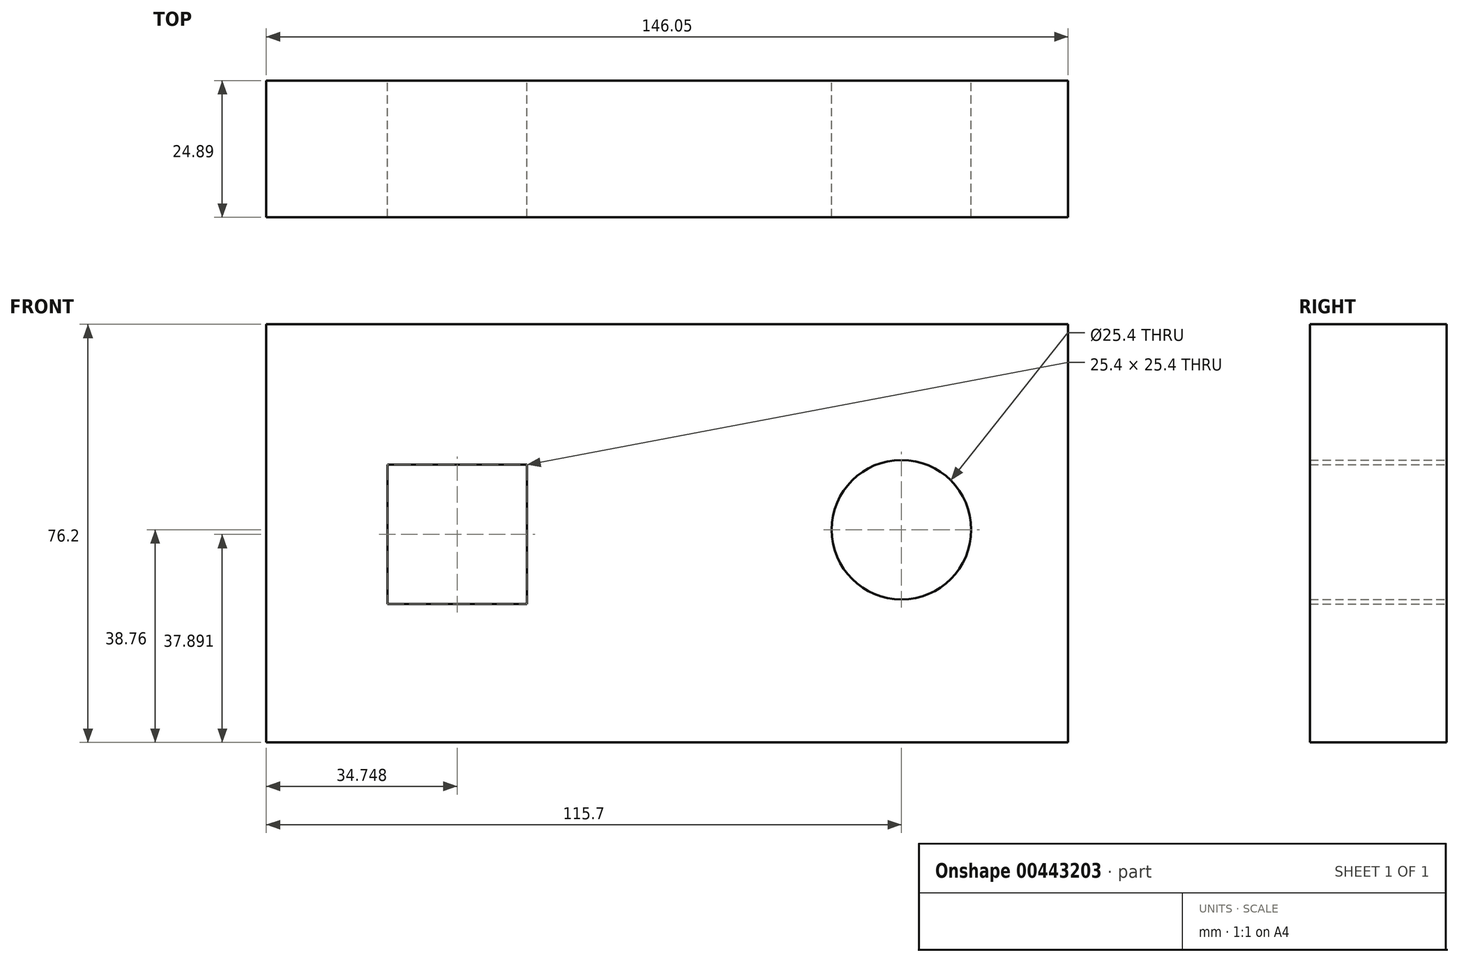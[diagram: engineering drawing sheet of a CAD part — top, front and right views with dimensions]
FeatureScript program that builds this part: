
annotation { "Feature Type Name" : "Feature", "Feature Type Description" : "" }
export const myFeature = defineFeature(function(context is Context, id is Id, definition is map)
    precondition{}
    {
        {
            var Q0;
            Q0=qCreatedBy(makeId("Front.planeOp"),FACE);
            var sketch = newSketch(context, id + "F0", { "sketchPlane" : qUnion([Q0])});
            skLineSegment(sketch, "E0.bottom", {"start": v(-115.7, 37.44) * mm, "end": v(30.35, 37.44) * mm});
            skLineSegment(sketch, "E0.top", {"start": v(-115.7, -38.76) * mm, "end": v(30.35, -38.76) * mm});
            skLineSegment(sketch, "E0.left", {"start": v(-115.7, 37.44) * mm, "end": v(-115.7, -38.76) * mm});
            skLineSegment(sketch, "E0.right", {"start": v(30.35, 37.44) * mm, "end": v(30.35, -38.76) * mm});
            skCircle(sketch, "E1", {"center": v(0, 0) * mm, "radius": 12.7 * mm});
            skLineSegment(sketch, "E2.bottom", {"start": v(-93.65, 11.83) * mm, "end": v(-68.25, 11.83) * mm});
            skLineSegment(sketch, "E2.top", {"start": v(-93.65, -13.57) * mm, "end": v(-68.25, -13.57) * mm});
            skLineSegment(sketch, "E2.left", {"start": v(-93.65, 11.83) * mm, "end": v(-93.65, -13.57) * mm});
            skLineSegment(sketch, "E2.right", {"start": v(-68.25, 11.83) * mm, "end": v(-68.25, -13.57) * mm});
            skPoint(sketch, "E3.orphan", {"position": v(-42.68, -38.76) * mm});
            skPoint(sketch, "E4.start.orphan", {"position": v(-42.68, 37.44) * mm});
            skPoint(sketch, "E5.orphan", {"position": v(0, 34.74) * mm});
            skPoint(sketch, "E6.trimOffspring.end.orphan", {"position": v(-81.26, -38.76) * mm});
            skPoint(sketch, "E7.orphan", {"position": v(0, -38.76) * mm});
            skSolve(sketch);
        }
        {
            var Q0;
            Q0 = qSketchRegion(id + "F0", true);
            extrude(context, id + "F1", {"entities" : qUnion([Q0]), "depth" : 24.9 * mm});
        }
    });
